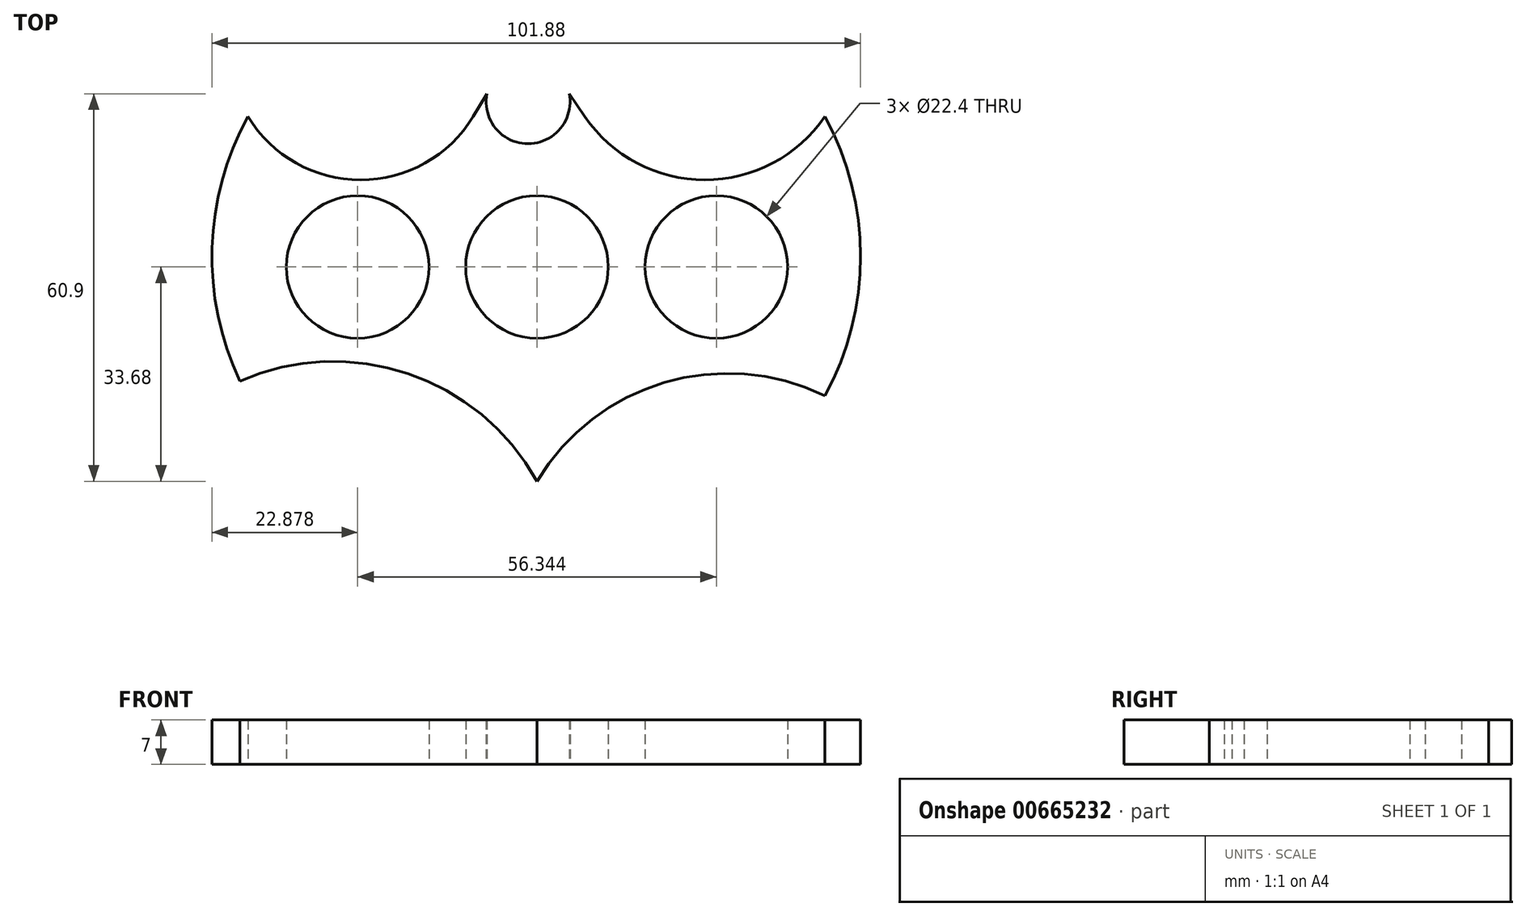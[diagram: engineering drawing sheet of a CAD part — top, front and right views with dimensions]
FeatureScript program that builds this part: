
annotation { "Feature Type Name" : "Feature", "Feature Type Description" : "" }
export const myFeature = defineFeature(function(context is Context, id is Id, definition is map)
    precondition{}
    {
        {
            var Q0;
            Q0=qCreatedBy(makeId("Top.planeOp"),FACE);
            var sketch = newSketch(context, id + "F0", { "sketchPlane" : qUnion([Q0])});
            skCircle(sketch, "E0", {"center": v(0, 0) * mm, "radius": 11.2 * mm});
            skCircle(sketch, "E1", {"center": v(28.17, 0) * mm, "radius": 11.2 * mm});
            skCircle(sketch, "E2.1.0", {"center": v(-28.17, 0) * mm, "radius": 11.2 * mm});
            skArc(sketch, "E3", {"start": v(-45.39, 23.62) * mm, "mid": v(-51.03, 3) * mm, "end": v(-46.68, -17.94) * mm});
            skArc(sketch, "E4", {"start": v(-45.39, 23.62) * mm, "mid": v(-27.7, 13.68) * mm, "end": v(-10.03, 23.62) * mm});
            skArc(sketch, "E5", {"start": v(7.52, 23.62) * mm, "mid": v(26.37, 13.67) * mm, "end": v(45.2, 23.62) * mm});
            skArc(sketch, "E6", {"start": v(45.2, -20.26) * mm, "mid": v(50.83, 1.68) * mm, "end": v(45.2, 23.62) * mm});
            skArc(sketch, "E7", {"start": v(0, -33.68) * mm, "mid": v(-20.28, -16.75) * mm, "end": v(-46.68, -17.94) * mm});
            skArc(sketch, "E8", {"start": v(45.2, -20.26) * mm, "mid": v(20, -18.17) * mm, "end": v(0, -33.68) * mm});
            skLineSegment(sketch, "E9", {"start": v(-10.03, 23.62) * mm, "end": v(-7.86, 27.17) * mm});
            skLineSegment(sketch, "E10", {"start": v(7.52, 23.62) * mm, "end": v(5.06, 27.22) * mm});
            skArc(sketch, "E11", {"start": v(-7.86, 27.17) * mm, "mid": v(-1.37, 19.36) * mm, "end": v(5.06, 27.22) * mm});
            skSolve(sketch);
        }
        {
            var Q0;
            Q0=makeQuery(id+"F0.imprint","IMPRINT",FACE,{"disambiguationData":[TD([[makeQuery(id+"F0.imprint","IMPRINT",EDGE,{"derivedFrom":sQuery(id+"F0.wireOp",EDGE,"E0")}),-1.0]])]});
            extrude(context, id + "F1", {"entities" : qUnion([Q0]), "depth" : 7 * mm, "offsetDistance" : 25 * mm});
        }
    });
